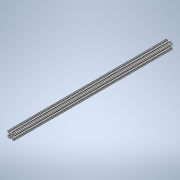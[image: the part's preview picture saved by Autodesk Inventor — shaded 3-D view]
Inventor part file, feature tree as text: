
AUTODESK INVENTOR PART (.ipt)
format: ipt  version: 2020 (Build 240168000, 168)  size: 238,592 bytes
history: native  units: in
note: dims shown in document units (in); Inventor stores cm internally (conversion verified against a paired STEP export)
features: extrude x1, sketch x1
ambient origin geometry x8: Origin, YZ Plane, XZ Plane, XY Plane, X Axis, Y Axis, Z Axis, Center Point
bodies: Solid1 (feature_tree)
feature tree (2):
  extrude  "Extrusion1"  [1 undecoded]
  sketch  "Sketch1"  dims[d0=24.0in d1=0.0in]
note: 1 required parameter value undecoded (feature->parameter linkage not recoverable at this tier; creation-order binding heuristic only, values carry confidence <= 0.55)
